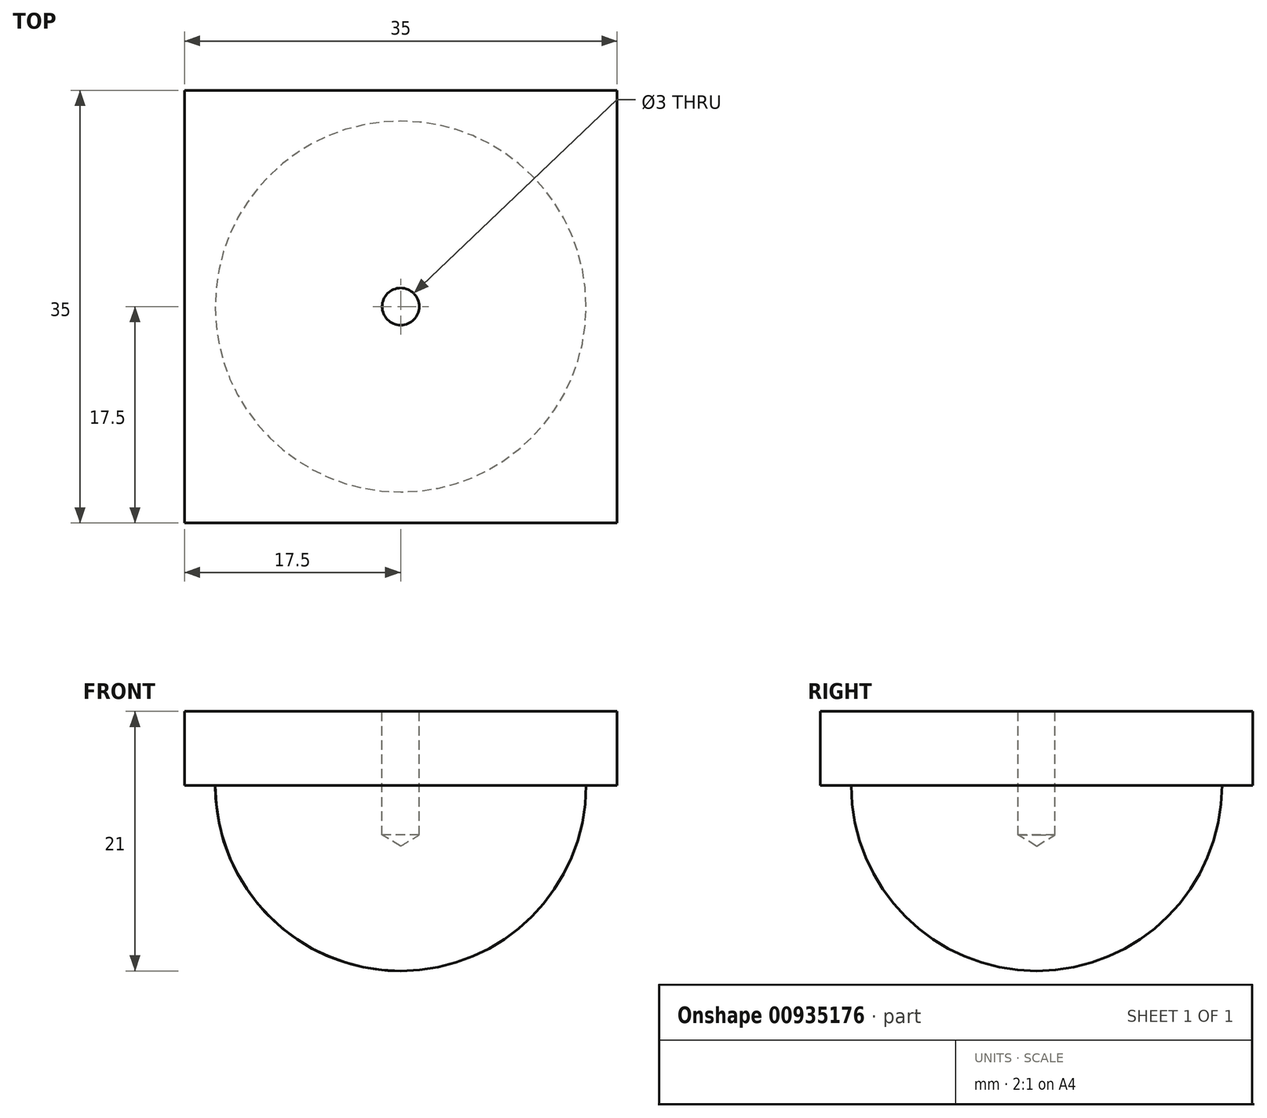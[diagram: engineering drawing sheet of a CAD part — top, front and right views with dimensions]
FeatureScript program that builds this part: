
annotation { "Feature Type Name" : "Feature", "Feature Type Description" : "" }
export const myFeature = defineFeature(function(context is Context, id is Id, definition is map)
    precondition{}
    {
        {
            var Q0;
            Q0=qCreatedBy(makeId("Top.planeOp"),FACE);
            var sketch = newSketch(context, id + "F0", { "sketchPlane" : qUnion([Q0])});
            skLineSegment(sketch, "E0.bottom", {"start": v(-17.5, -17.5) * mm, "end": v(17.5, -17.5) * mm});
            skLineSegment(sketch, "E0.top", {"start": v(-17.5, 17.5) * mm, "end": v(17.5, 17.5) * mm});
            skLineSegment(sketch, "E0.left", {"start": v(-17.5, -17.5) * mm, "end": v(-17.5, 17.5) * mm});
            skLineSegment(sketch, "E0.right", {"start": v(17.5, -17.5) * mm, "end": v(17.5, 17.5) * mm});
            skPoint(sketch, "E0.middle", {"position": v(0, 0) * mm});
            skSolve(sketch);
        }
        {
            var Q0;
            Q0=qSketchRegion(id+"F0",true);
            extrude(context, id + "F1", {"entities" : qUnion([Q0]), "oppositeDirection" : true, "depth" : 6 * mm, "offsetDistance" : 25 * mm});
        }
        {
            var Q0;
            Q0=qCreatedBy(makeId("Front.planeOp"),FACE);
            var sketch = newSketch(context, id + "F2", { "sketchPlane" : qUnion([Q0])});
            skPoint(sketch, "E1.0", {"position": v(0, -6) * mm});
            skArc(sketch, "E2", {"start": v(0, -21) * mm, "mid": v(10.6, -16.6) * mm, "end": v(15, -6) * mm});
            skLineSegment(sketch, "E3.0", {"start": v(0, -6) * mm, "end": v(15, -6) * mm});
            skPoint(sketch, "E4", {"position": v(15, -6) * mm});
            skLineSegment(sketch, "E5", {"start": v(0, -6) * mm, "end": v(0, -21) * mm});
            skSolve(sketch);
        }
        {
            var Q0;
            Q0=qSketchRegion(id+"F2",true);
            var Q1;
            Q1=sQuery(id+"F2.wireOp",EDGE,"E5");
            revolve(context, id + "F3", {"operationType" : NewBodyOperationType.ADD, "surfaceOperationType" : NewSurfaceOperationType.NEW, "entities" : qUnion([Q0]), "axis" : qUnion([Q1]), "revolveType" : RevolveType.FULL});
        }
        {
            var Q0;
            Q0=sQuery(id+"F0.wireOp",VERTEX,"E0.middle");
            var Q1;
            Q1=makeQuery(id+"F1.opExtrude","SWEPT_BODY",BODY,{"disambiguationData":[OSD([sQuery(id+"F0.wireOp",EDGE,"E0.bottom"),sQuery(id+"F0.wireOp",EDGE,"E0.top"),sQuery(id+"F0.wireOp",EDGE,"E0.left"),sQuery(id+"F0.wireOp",EDGE,"E0.right")])]});
            hole(context, id + "F4", {"style" : HoleStyle.SIMPLE, "endStyle" : HoleEndStyle.BLIND, "standardTappedOrClearance" : lookupTablePath({ "standard" : "ISO", "size" : "3", "type" : "Drilled" }), "standardBlindInLast" : lookupTablePath({ "standard" : "ISO", "size" : "3", "type" : "Drilled" }), "holeDiameter" : 3 * mm, "majorDiameter" : 5 * mm, "holeDepth" : 10 * mm, "tappedDepth" : 15 * mm, "tapClearance" : 3, "locations" : qUnion([Q0]), "scope" : qUnion([Q1])});
        }
    });
